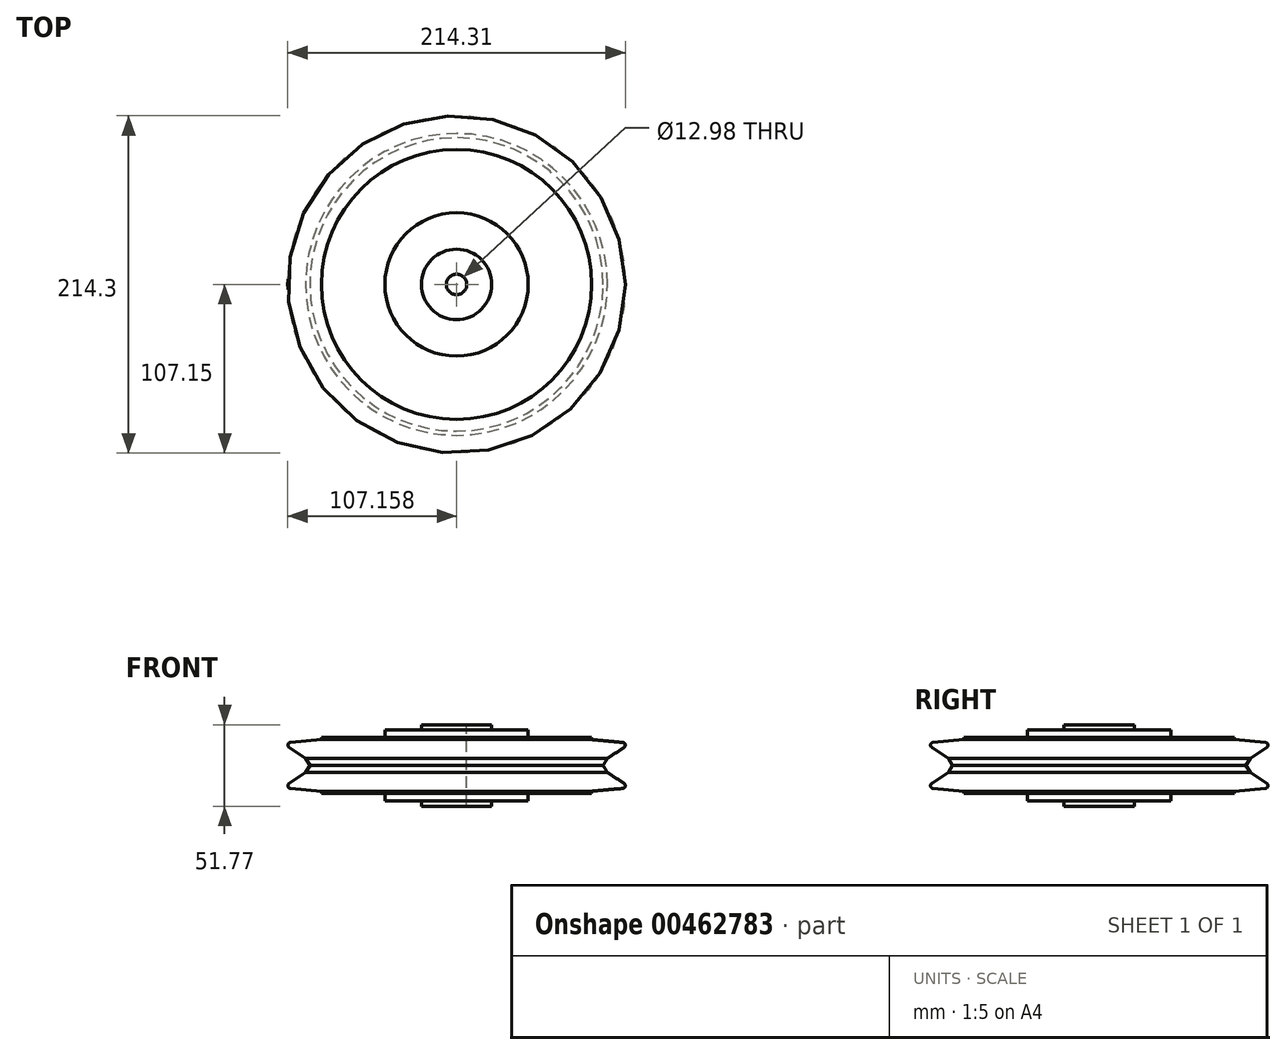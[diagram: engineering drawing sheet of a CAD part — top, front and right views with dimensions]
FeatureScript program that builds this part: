
annotation { "Feature Type Name" : "Feature", "Feature Type Description" : "" }
export const myFeature = defineFeature(function(context is Context, id is Id, definition is map)
    precondition{}
    {
        {
            var Q0;
            Q0=qCreatedBy(makeId("Front.planeOp"),FACE);
            var sketch = newSketch(context, id + "F0", { "sketchPlane" : qUnion([Q0])});
            skLineSegment(sketch, "E0", {"start": v(206.6, -50.95) * mm, "end": v(119.93, -50.95) * mm});
            skLineSegment(sketch, "E1", {"start": v(119.93, -50.95) * mm, "end": v(119.93, -25.06) * mm});
            skLineSegment(sketch, "E2", {"start": v(119.93, -25.06) * mm, "end": v(135.78, -25.06) * mm});
            skLineSegment(sketch, "E3", {"start": v(135.78, -25.06) * mm, "end": v(135.78, -28.32) * mm});
            skLineSegment(sketch, "E4", {"start": v(135.78, -28.32) * mm, "end": v(158.95, -28.32) * mm});
            skLineSegment(sketch, "E5", {"start": v(158.95, -28.32) * mm, "end": v(158.95, -33.03) * mm});
            skLineSegment(sketch, "E6", {"start": v(158.95, -33.03) * mm, "end": v(199.22, -33.03) * mm});
            skLineSegment(sketch, "E7", {"start": v(199.22, -33.03) * mm, "end": v(199.22, -34.55) * mm});
            skLineSegment(sketch, "E8", {"start": v(199.22, -34.55) * mm, "end": v(219, -36.35) * mm});
            skArc(sketch, "E9", {"start": v(219, -36.35) * mm, "mid": v(220.54, -37.66) * mm, "end": v(219.8, -39.54) * mm});
            skLineSegment(sketch, "E10", {"start": v(219.8, -39.54) * mm, "end": v(209.3, -46.43) * mm});
            skLineSegment(sketch, "E11", {"start": v(209.3, -46.43) * mm, "end": v(206.6, -50.95) * mm});
            skLineSegment(sketch, "E12", {"start": v(113.44, -2.59) * mm, "end": v(113.44, -61.47) * mm, "construction": true});
            skSolve(sketch);
        }
        {
            var Q0;
            Q0=makeQuery(id+"F0.imprint","IMPRINT",FACE,{"disambiguationData":[TD([[makeQuery(id+"F0.imprint","IMPRINT",EDGE,{"derivedFrom":sQuery(id+"F0.wireOp",EDGE,"E0")}),-1.0]])]});
            var Q1;
            Q1=sQuery(id+"F0.wireOp",EDGE,"E12");
            var Q2;
            Q2=sQuery(id+"F0.wireOp",EDGE,"E10");
            var Q3;
            Q3=sQuery(id+"F0.wireOp",EDGE,"E12");
            revolve(context, id + "F1", {"entities" : qUnion([Q0]), "surfaceEntities" : qUnion([Q1, Q2]), "axis" : qUnion([Q3]), "revolveType" : RevolveType.FULL});
        }
        {
            var Q0;
            Q0=makeQuery(id+"F1.opRevolve","SWEPT_BODY",BODY,{"disambiguationData":[OSD([sQuery(id+"F0.wireOp",EDGE,"E0"),sQuery(id+"F0.wireOp",EDGE,"E1"),sQuery(id+"F0.wireOp",EDGE,"E2"),sQuery(id+"F0.wireOp",EDGE,"E3"),sQuery(id+"F0.wireOp",EDGE,"E4"),sQuery(id+"F0.wireOp",EDGE,"E5"),sQuery(id+"F0.wireOp",EDGE,"E6"),sQuery(id+"F0.wireOp",EDGE,"E7"),sQuery(id+"F0.wireOp",EDGE,"E8"),sQuery(id+"F0.wireOp",EDGE,"E9"),sQuery(id+"F0.wireOp",EDGE,"E10"),sQuery(id+"F0.wireOp",EDGE,"E11")])]});
            var Q1;
            Q1=makeQuery(id+"F1.opRevolve","SWEPT_FACE",FACE,{"disambiguationData":[OSD([sQuery(id+"F0.wireOp",EDGE,"E0")])]});
            mirror(context, id + "F2", {"operationType" : NewBodyOperationType.ADD, "entities" : qUnion([Q0]), "mirrorPlane" : qUnion([Q1])});
        }
    });
